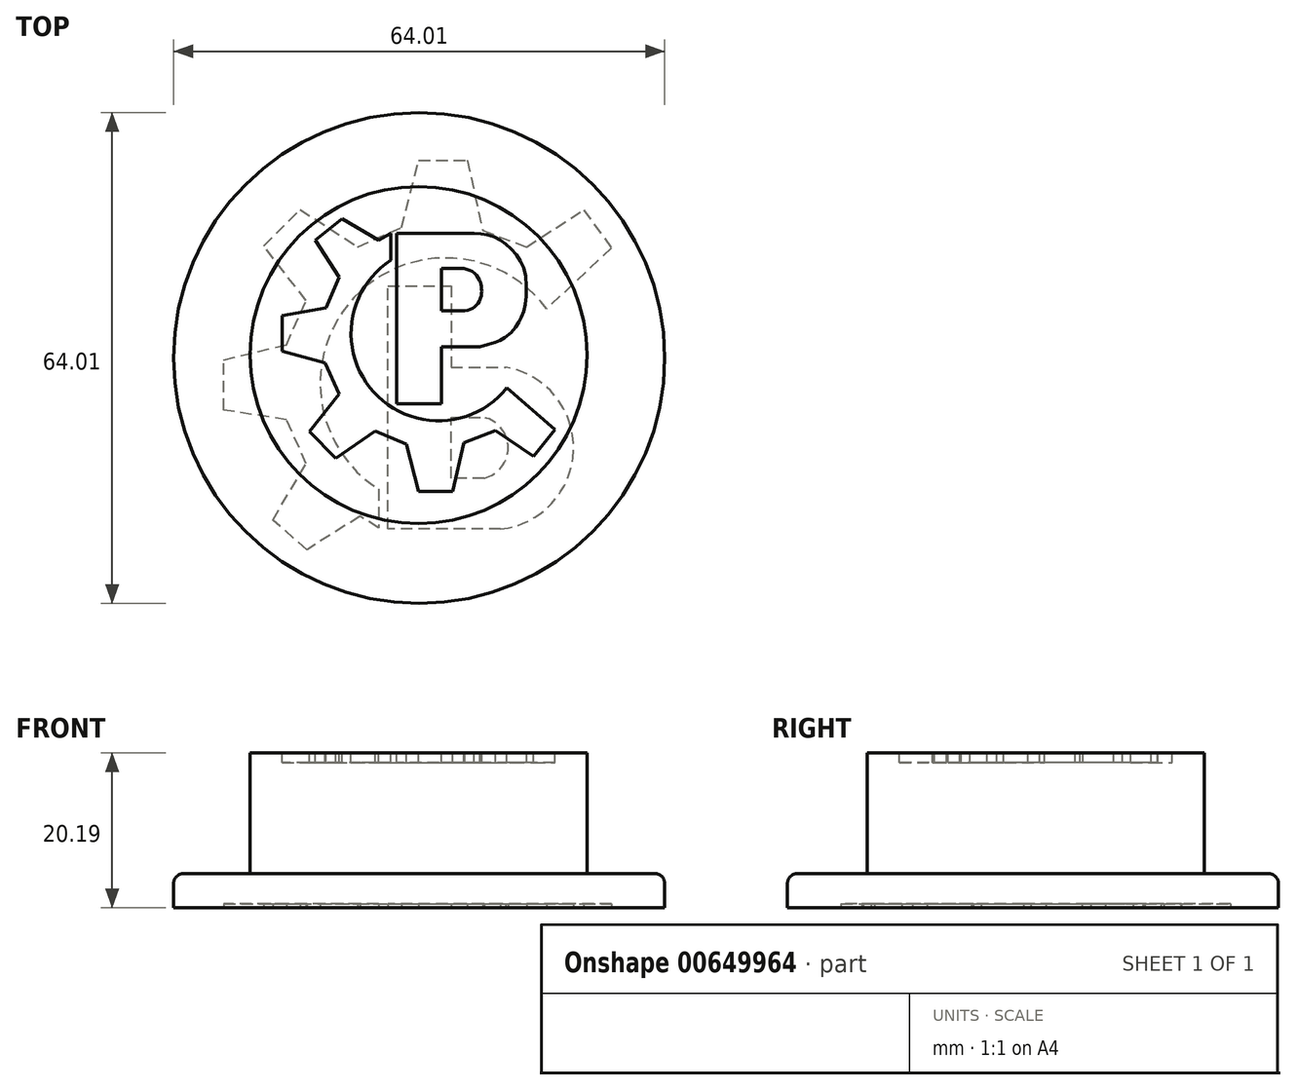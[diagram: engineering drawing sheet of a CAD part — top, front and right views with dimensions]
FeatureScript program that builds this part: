
annotation { "Feature Type Name" : "Feature", "Feature Type Description" : "" }
export const myFeature = defineFeature(function(context is Context, id is Id, definition is map)
    precondition{}
    {
        {
            var Q0;
            Q0=qCreatedBy(makeId("Top.planeOp"),FACE);
            var sketch = newSketch(context, id + "F0", { "sketchPlane" : qUnion([Q0])});
            skCircle(sketch, "E0", {"center": v(0.07, -0.4) * mm, "radius": 32 * mm});
            skSolve(sketch);
        }
        {
            var Q0;
            Q0=makeQuery(id+"F0.imprint","IMPRINT",FACE,{"disambiguationData":[TD([[makeQuery(id+"F0.imprint","IMPRINT",EDGE,{"derivedFrom":sQuery(id+"F0.wireOp",EDGE,"E0")}),1.0]])]});
            extrude(context, id + "F1", {"entities" : qUnion([Q0]), "depth" : 4.44 * mm, "offsetDistance" : 25.4 * mm});
        }
        {
            var Q0;
            Q0=makeQuery(id+"F1.opExtrude","CAP_FACE",FACE,{"disambiguationData":[OSD([sQuery(id+"F0.wireOp",EDGE,"E0")])],"isStart":false});
            var sketch = newSketch(context, id + "F2", { "sketchPlane" : qUnion([Q0])});
            skCircle(sketch, "E1", {"center": v(0, 0) * mm, "radius": 21.97 * mm});
            skSolve(sketch);
        }
        {
            var Q0;
            Q0=qSketchRegion(id+"F2",true);
            extrude(context, id + "F3", {"entities" : qUnion([Q0]), "operationType" : NewBodyOperationType.ADD, "depth" : 15.75 * mm, "offsetDistance" : 25.4 * mm});
        }
        {
            var Q0;
            Q0=makeQuery(id+"F1.opExtrude","CAP_EDGE",EDGE,{"disambiguationData":[OSD([sQuery(id+"F0.wireOp",EDGE,"E0")])],"isStart":false});
            fillet(context, id + "F4", {"entities" : qUnion([Q0]), "radius" : 1.27 * mm, "tangentPropagation" : true, "allowEdgeOverflow" : false});
        }
        {
            var Q0;
            Q0=makeQuery(id+"F3.opExtrude","CAP_FACE",FACE,{"disambiguationData":[OSD([sQuery(id+"F2.wireOp",EDGE,"E1")])],"isStart":false});
            var sketch = newSketch(context, id + "F5", { "sketchPlane" : qUnion([Q0])});
            skLineSegment(sketch, "E2", {"start": v(7.26, 15.88) * mm, "end": v(-2.87, 15.88) * mm});
            skLineSegment(sketch, "E3", {"start": v(-2.87, 15.88) * mm, "end": v(-2.87, -6.38) * mm});
            skLineSegment(sketch, "E4", {"start": v(-2.87, -6.38) * mm, "end": v(2.97, -6.38) * mm});
            skLineSegment(sketch, "E5", {"start": v(2.97, -6.38) * mm, "end": v(2.97, 1.09) * mm});
            skLineSegment(sketch, "E6", {"start": v(2.97, 1.09) * mm, "end": v(8, 1.09) * mm});
            skLineSegment(sketch, "E7", {"start": v(5.9, 11.26) * mm, "end": v(3, 11.26) * mm});
            skLineSegment(sketch, "E8", {"start": v(3, 11.26) * mm, "end": v(3, 5.74) * mm});
            skLineSegment(sketch, "E9", {"start": v(3, 5.74) * mm, "end": v(6.03, 5.74) * mm});
            skFitSpline(sketch, "E10", {"points": [v(5.9, 11.26) * mm, v(7.05, 10.84) * mm, v(7.81, 9.96) * mm, v(8.12, 9.25) * mm, v(8.22, 8.42) * mm, v(8.15, 7.68) * mm, v(7.67, 6.64) * mm, v(7.02, 6.08) * mm, v(6.03, 5.74) * mm], "startDerivative": vector(8.7, -2.02) * mm, "endDerivative": vector(-8.15, -2.2) * mm});
            skFitSpline(sketch, "E11", {"points": [v(7.26, 15.88) * mm, v(8.78, 15.72) * mm, v(10.37, 15.16) * mm, v(11.76, 14.17) * mm, v(13.07, 12.6) * mm, v(13.86, 10.72) * mm, v(14.01, 7.33) * mm, v(13.63, 5.49) * mm, v(13.1, 4.38) * mm, v(12.36, 3.2) * mm, v(10.87, 2.05) * mm, v(10, 1.66) * mm, v(8, 1.09) * mm], "startDerivative": vector(19.48, -1.1) * mm, "endDerivative": vector(-25.02, -6.78) * mm});
            skArc(sketch, "E12", {"start": v(-3.63, 12.36) * mm, "mid": v(-5.83, -4.86) * mm, "end": v(11.52, -4.25) * mm});
            skPoint(sketch, "E12.first.point", {"position": v(-3.63, 12.36) * mm});
            skPoint(sketch, "E12.second.point", {"position": v(-8.8, 2.54) * mm});
            skPoint(sketch, "E12.third.point", {"position": v(11.52, -4.25) * mm});
            skLineSegment(sketch, "E13", {"start": v(-3.63, 12.36) * mm, "end": v(-3.63, 15.87) * mm});
            skLineSegment(sketch, "E14", {"start": v(-3.63, 15.87) * mm, "end": v(-5.24, 15) * mm});
            skLineSegment(sketch, "E15", {"start": v(-5.24, 15) * mm, "end": v(-9.98, 17.78) * mm});
            skLineSegment(sketch, "E16", {"start": v(-9.98, 17.78) * mm, "end": v(-13.44, 15) * mm});
            skLineSegment(sketch, "E17", {"start": v(-13.44, 15) * mm, "end": v(-10.37, 10.16) * mm});
            skLineSegment(sketch, "E18", {"start": v(-10.37, 10.16) * mm, "end": v(-12.08, 6.15) * mm});
            skLineSegment(sketch, "E19", {"start": v(-12.08, 6.15) * mm, "end": v(-17.78, 5.13) * mm});
            skLineSegment(sketch, "E20", {"start": v(-17.78, 5.13) * mm, "end": v(-17.78, 0.49) * mm});
            skLineSegment(sketch, "E21", {"start": v(-17.78, 0.49) * mm, "end": v(-12.17, -1.03) * mm});
            skLineSegment(sketch, "E22", {"start": v(-12.17, -1.03) * mm, "end": v(-10.37, -5.08) * mm});
            skLineSegment(sketch, "E23", {"start": v(-10.37, -5.08) * mm, "end": v(-14.23, -9.97) * mm});
            skLineSegment(sketch, "E24", {"start": v(-14.23, -9.97) * mm, "end": v(-10.8, -13.48) * mm});
            skLineSegment(sketch, "E25", {"start": v(-10.8, -13.48) * mm, "end": v(-5.63, -9.92) * mm});
            skLineSegment(sketch, "E26", {"start": v(-5.63, -9.92) * mm, "end": v(-1.62, -11.63) * mm});
            skLineSegment(sketch, "E27", {"start": v(-1.62, -11.63) * mm, "end": v(0, -17.78) * mm});
            skLineSegment(sketch, "E28", {"start": v(0, -17.78) * mm, "end": v(4.43, -17.78) * mm});
            skLineSegment(sketch, "E29", {"start": v(4.43, -17.78) * mm, "end": v(5.9, -11.43) * mm});
            skLineSegment(sketch, "E30", {"start": v(5.9, -11.43) * mm, "end": v(10, -9.87) * mm});
            skLineSegment(sketch, "E31", {"start": v(10, -9.87) * mm, "end": v(14.98, -13.24) * mm});
            skLineSegment(sketch, "E32", {"start": v(14.98, -13.24) * mm, "end": v(17.78, -9.72) * mm});
            skLineSegment(sketch, "E33", {"start": v(17.78, -9.72) * mm, "end": v(11.52, -4.25) * mm});
            skSolve(sketch);
        }
        {
            var Q0;
            Q0=makeQuery(id+"F5.imprint","IMPRINT",FACE,{"disambiguationData":[TD([[makeQuery(id+"F5.imprint","IMPRINT",EDGE,{"derivedFrom":sQuery(id+"F5.wireOp",EDGE,"E12")}),-1.0]])]});
            var Q1;
            Q1=makeQuery(id+"F5.imprint","IMPRINT",FACE,{"disambiguationData":[TD([[makeQuery(id+"F5.imprint","IMPRINT",EDGE,{"derivedFrom":sQuery(id+"F5.wireOp",EDGE,"E2")}),1.0]])]});
            extrude(context, id + "F6", {"entities" : qUnion([Q0, Q1]), "operationType" : NewBodyOperationType.REMOVE, "oppositeDirection" : true, "depth" : 1.27 * mm, "offsetDistance" : 25.4 * mm});
        }
        {
            var Q0;
            Q0=makeQuery(id+"F1.opExtrude","CAP_FACE",FACE,{"disambiguationData":[OSD([sQuery(id+"F0.wireOp",EDGE,"E0")])],"isStart":true});
            var sketch = newSketch(context, id + "F7", { "sketchPlane" : qUnion([Q0])});
            skLineSegment(sketch, "E34", {"start": v(10.69, 22.7) * mm, "end": v(-4, 22.7) * mm});
            skLineSegment(sketch, "E35", {"start": v(-4, 22.7) * mm, "end": v(-4, -9.02) * mm});
            skLineSegment(sketch, "E36", {"start": v(-4, -9.02) * mm, "end": v(4.24, -9.02) * mm});
            skLineSegment(sketch, "E37", {"start": v(4.24, -9.02) * mm, "end": v(4.24, 1.6) * mm});
            skLineSegment(sketch, "E38", {"start": v(4.24, 1.6) * mm, "end": v(11.36, 1.6) * mm});
            skArc(sketch, "E39", {"start": v(11.36, 1.6) * mm, "mid": v(20.2, 12.45) * mm, "end": v(10.69, 22.7) * mm});
            skPoint(sketch, "E39.second.point", {"position": v(20.02, 14.06) * mm});
            skLineSegment(sketch, "E40", {"start": v(8.56, 16.07) * mm, "end": v(4.24, 16.07) * mm});
            skLineSegment(sketch, "E41", {"start": v(4.24, 16.07) * mm, "end": v(4.24, 8.14) * mm});
            skLineSegment(sketch, "E42", {"start": v(4.24, 8.14) * mm, "end": v(8.56, 8.14) * mm});
            skArc(sketch, "E43", {"start": v(8.56, 8.14) * mm, "mid": v(11.67, 12.1) * mm, "end": v(8.56, 16.07) * mm});
            skPoint(sketch, "E43.second.point", {"position": v(11.67, 12.08) * mm});
            skLineSegment(sketch, "E44", {"start": v(-5.21, 17.5) * mm, "end": v(-5.21, 22.53) * mm});
            skLineSegment(sketch, "E45", {"start": v(-5.21, 22.53) * mm, "end": v(-7.65, 21.04) * mm});
            skLineSegment(sketch, "E46", {"start": v(-7.65, 21.04) * mm, "end": v(-14.57, 25.4) * mm});
            skLineSegment(sketch, "E47", {"start": v(-14.57, 25.4) * mm, "end": v(-19, 21.5) * mm});
            skLineSegment(sketch, "E48", {"start": v(-19, 21.5) * mm, "end": v(-14.65, 14.2) * mm});
            skLineSegment(sketch, "E49", {"start": v(-14.65, 14.2) * mm, "end": v(-17.2, 8.44) * mm});
            skLineSegment(sketch, "E50", {"start": v(-17.2, 8.44) * mm, "end": v(-25.4, 7.16) * mm});
            skLineSegment(sketch, "E51", {"start": v(-25.4, 7.16) * mm, "end": v(-25.4, 0.64) * mm});
            skLineSegment(sketch, "E52", {"start": v(-25.4, 0.64) * mm, "end": v(-17.24, -1.34) * mm});
            skLineSegment(sketch, "E53", {"start": v(-17.24, -1.34) * mm, "end": v(-14.65, -7.12) * mm});
            skLineSegment(sketch, "E54", {"start": v(-14.65, -7.12) * mm, "end": v(-20.18, -14.2) * mm});
            skLineSegment(sketch, "E55", {"start": v(-20.18, -14.2) * mm, "end": v(-15.47, -18.98) * mm});
            skLineSegment(sketch, "E56", {"start": v(-15.47, -18.98) * mm, "end": v(-7.92, -14.1) * mm});
            skLineSegment(sketch, "E57", {"start": v(-7.92, -14.1) * mm, "end": v(-2.2, -16.64) * mm});
            skLineSegment(sketch, "E58", {"start": v(-2.2, -16.64) * mm, "end": v(0, -25.4) * mm});
            skLineSegment(sketch, "E59", {"start": v(0, -25.4) * mm, "end": v(6.34, -25.4) * mm});
            skLineSegment(sketch, "E60", {"start": v(6.34, -25.4) * mm, "end": v(8.35, -16.27) * mm});
            skLineSegment(sketch, "E61", {"start": v(8.35, -16.27) * mm, "end": v(14.06, -14.08) * mm});
            skLineSegment(sketch, "E62", {"start": v(14.06, -14.08) * mm, "end": v(21.52, -18.92) * mm});
            skLineSegment(sketch, "E63", {"start": v(21.52, -18.92) * mm, "end": v(25.13, -13.97) * mm});
            skLineSegment(sketch, "E64", {"start": v(25.13, -13.97) * mm, "end": v(16.68, -6) * mm});
            skArc(sketch, "E65", {"start": v(-5.21, 17.5) * mm, "mid": v(-8.44, -7.45) * mm, "end": v(16.68, -6) * mm});
            skPoint(sketch, "E65.second.point", {"position": v(-12.06, -1.25) * mm});
            skSolve(sketch);
        }
        {
            var Q0;
            Q0 = qSketchRegion(id + "F7", true);
            var Q1;
            Q1=makeQuery(id+"F7.imprint","IMPRINT",FACE,{"disambiguationData":[TD([[makeQuery(id+"F7.imprint","IMPRINT",EDGE,{"derivedFrom":sQuery(id+"F7.wireOp",EDGE,"E44")}),1.0]])]});
            var Q2;
            Q2=makeQuery(id+"F7.imprint","IMPRINT",FACE,{"disambiguationData":[TD([[makeQuery(id+"F7.imprint","IMPRINT",EDGE,{"derivedFrom":sQuery(id+"F7.wireOp",EDGE,"E34")}),1.0]])]});
            extrude(context, id + "F8", {"entities" : qUnion([Q0, Q1, Q2]), "operationType" : NewBodyOperationType.REMOVE, "oppositeDirection" : true, "depth" : 0.5 * mm, "offsetDistance" : 25.4 * mm});
        }
    });
